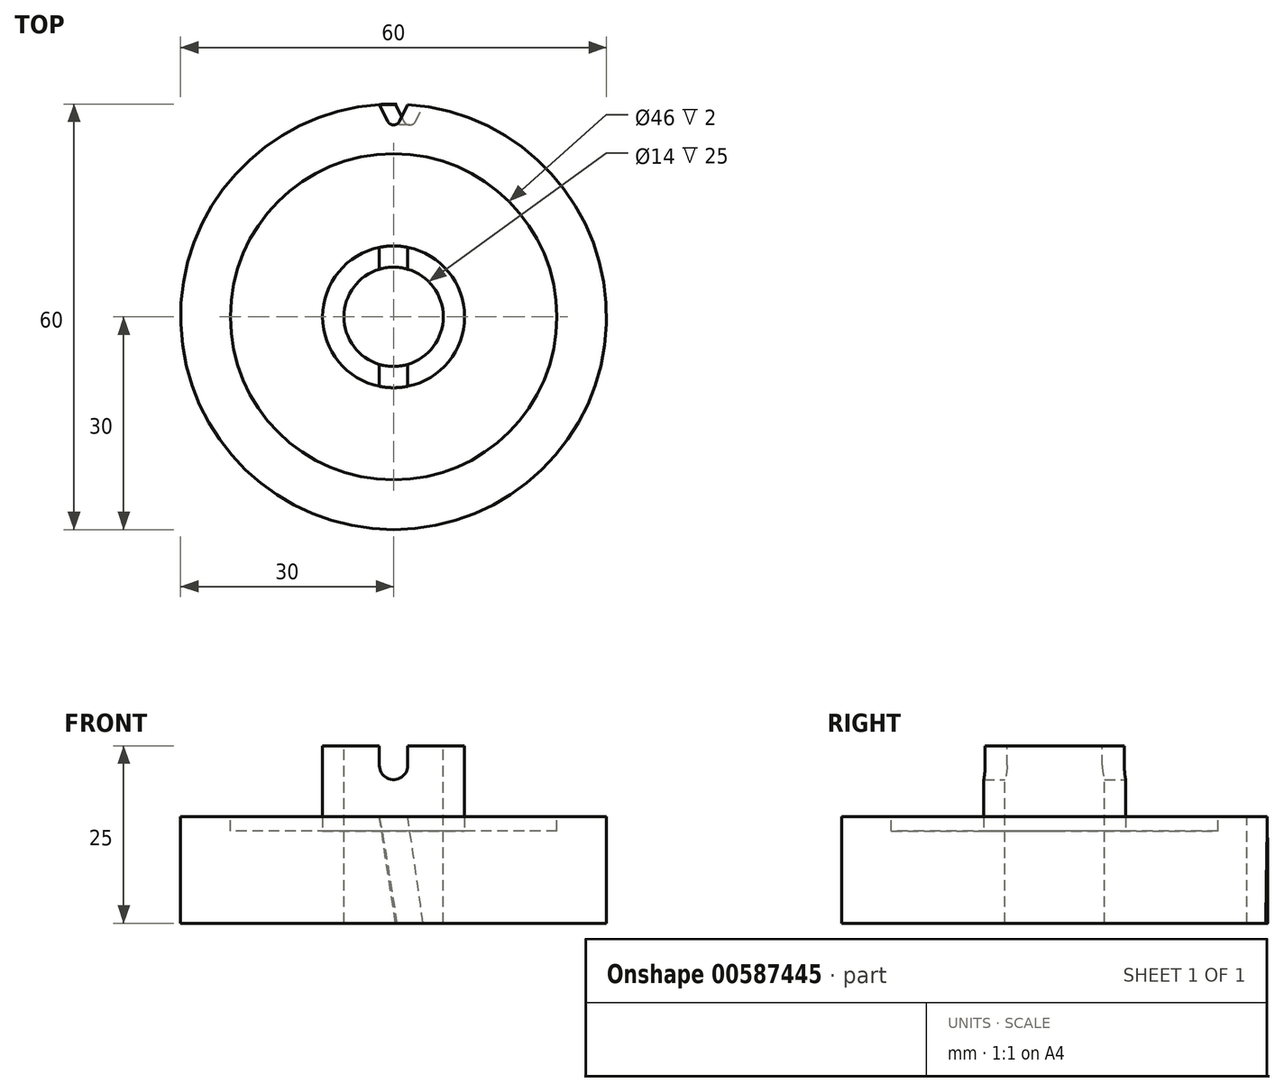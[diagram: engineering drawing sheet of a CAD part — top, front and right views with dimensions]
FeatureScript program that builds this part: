
annotation { "Feature Type Name" : "Feature", "Feature Type Description" : "" }
export const myFeature = defineFeature(function(context is Context, id is Id, definition is map)
    precondition{}
    {
        {
            var Q0;
            Q0=qCreatedBy(makeId("Top.planeOp"),FACE);
            var sketch = newSketch(context, id + "F0", { "sketchPlane" : qUnion([Q0])});
            skCircle(sketch, "E0", {"center": v(0, 0) * mm, "radius": 30 * mm});
            skSolve(sketch);
        }
        {
            var Q0;
            Q0 = qSketchRegion(id + "F0", true);
            extrude(context, id + "F1", {"entities" : qUnion([Q0]), "depth" : 15 * mm, "offsetDistance" : 25 * mm});
        }
        {
            var Q0;
            Q0=makeQuery(id+"F1.opExtrude","CAP_FACE",FACE,{"disambiguationData":[OSD([sQuery(id+"F0.wireOp",EDGE,"E0")])],"isStart":false});
            var sketch = newSketch(context, id + "F2", { "sketchPlane" : qUnion([Q0])});
            skCircle(sketch, "E1.0", {"center": v(0, 0) * mm, "radius": 23 * mm});
            skSolve(sketch);
        }
        {
            var Q0;
            Q0 = qSketchRegion(id + "F2", true);
            extrude(context, id + "F3", {"entities" : qUnion([Q0]), "operationType" : NewBodyOperationType.REMOVE, "oppositeDirection" : true, "depth" : 2 * mm, "offsetDistance" : 25 * mm});
        }
        {
            var Q0;
            Q0=makeQuery(id+"F3.boolean.opBoolean","COPY",FACE,{"derivedFrom":makeQuery(id+"F3.opExtrude","CAP_FACE",FACE,{"disambiguationData":[OSD([sQuery(id+"F2.wireOp",EDGE,"E1.0")])],"isStart":false})});
            var sketch = newSketch(context, id + "F4", { "sketchPlane" : qUnion([Q0])});
            skCircle(sketch, "E2", {"center": v(0, 0) * mm, "radius": 10 * mm});
            skSolve(sketch);
        }
        {
            var Q0;
            Q0=makeQuery(id+"F4.imprint","IMPRINT",FACE,{"disambiguationData":[TD([[makeQuery(id+"F4.imprint","IMPRINT",EDGE,{"derivedFrom":sQuery(id+"F4.wireOp",EDGE,"E2")}),1.0]])]});
            extrude(context, id + "F5", {"entities" : qUnion([Q0]), "operationType" : NewBodyOperationType.ADD, "depth" : 12 * mm, "offsetDistance" : 25 * mm});
        }
        {
            var Q0;
            Q0=makeQuery(id+"F5.opExtrude","CAP_FACE",FACE,{"disambiguationData":[OSD([sQuery(id+"F4.wireOp",EDGE,"E2")])],"isStart":false});
            var sketch = newSketch(context, id + "F6", { "sketchPlane" : qUnion([Q0])});
            skCircle(sketch, "E3.0", {"center": v(0, 0) * mm, "radius": 7 * mm});
            skSolve(sketch);
        }
        {
            var Q0;
            Q0=makeQuery(id+"F6.imprint","IMPRINT",FACE,{"disambiguationData":[TD([[makeQuery(id+"F6.imprint","IMPRINT",EDGE,{"derivedFrom":sQuery(id+"F6.wireOp",EDGE,"E3.0")}),1.0]])]});
            extrude(context, id + "F7", {"entities" : qUnion([Q0]), "operationType" : NewBodyOperationType.REMOVE, "oppositeDirection" : true, "depth" : 45.4 * mm, "offsetDistance" : 25 * mm});
        }
        {
            var Q0;
            Q0=qCreatedBy(makeId("Front.planeOp"),FACE);
            var sketch = newSketch(context, id + "F8", { "sketchPlane" : qUnion([Q0])});
            skLineSegment(sketch, "E4.bottom", {"start": v(2, 26.24) * mm, "end": v(-2, 26.24) * mm});
            skLineSegment(sketch, "E4.left", {"start": v(2, 26.24) * mm, "end": v(2, 22.24) * mm});
            skLineSegment(sketch, "E4.right", {"start": v(-2, 26.24) * mm, "end": v(-2, 22.24) * mm});
            skPoint(sketch, "E4.middle", {"position": v(0, 24.24) * mm});
            skArc(sketch, "E5", {"start": v(-2, 22.24) * mm, "mid": v(0, 20.24) * mm, "end": v(2, 22.24) * mm});
            skSolve(sketch);
        }
        {
            var Q0;
            Q0=makeQuery(id+"F8.imprint","IMPRINT",FACE,{"disambiguationData":[TD([[makeQuery(id+"F8.imprint","IMPRINT",EDGE,{"derivedFrom":sQuery(id+"F8.wireOp",EDGE,"E4.bottom")}),1.0]])]});
            extrude(context, id + "F9", {"entities" : qUnion([Q0]), "operationType" : NewBodyOperationType.REMOVE, "endBound" : BoundingType.SYMMETRIC, "depth" : 25 * mm, "offsetDistance" : 25 * mm});
        }
        {
            var Q0;
            Q0=makeQuery(id+"F1.opExtrude","CAP_FACE",FACE,{"disambiguationData":[OSD([sQuery(id+"F0.wireOp",EDGE,"E0")])],"isStart":false});
            var sketch = newSketch(context, id + "F10", { "sketchPlane" : qUnion([Q0])});
            skArc(sketch, "E6", {"start": v(-0.85, 27.58) * mm, "mid": v(0, 27.06) * mm, "end": v(0.85, 27.58) * mm});
            skLineSegment(sketch, "E7", {"start": v(0.85, 27.58) * mm, "end": v(2, 29.93) * mm});
            skLineSegment(sketch, "E8", {"start": v(0, 30.67) * mm, "end": v(0, 25.54) * mm, "construction": true});
            skLineSegment(sketch, "E9.MirrorCS", {"start": v(-0.85, 27.58) * mm, "end": v(-2, 29.93) * mm});
            skArc(sketch, "E10", {"start": v(2, 29.93) * mm, "mid": v(0, 30.34) * mm, "end": v(-2, 29.93) * mm});
            skSolve(sketch);
        }
        {
            var Q0;
            Q0=qCreatedBy(makeId("Front.planeOp"),FACE);
            var sketch = newSketch(context, id + "F11", { "sketchPlane" : qUnion([Q0])});
            skLineSegment(sketch, "E11", {"start": v(0, -1.28) * mm, "end": v(0, 15.72) * mm});
            skLineSegment(sketch, "E12", {"start": v(0, -1.28) * mm, "end": v(-2.57, 15.72) * mm});
            skLineSegment(sketch, "E13", {"start": v(-2.57, 15.72) * mm, "end": v(0, 15.72) * mm});
            skSolve(sketch);
        }
        {
            var Q0;
            Q0=makeQuery(id+"F10.imprint","IMPRINT",FACE,{"disambiguationData":[TD([[makeQuery(id+"F10.imprint","IMPRINT",EDGE,{"derivedFrom":sQuery(id+"F10.wireOp",EDGE,"E6")}),1.0]])]});
            var Q1;
            {var subQ0=sQuery(id+"F10.wireOp",EDGE,"E10");Q1=makeQuery(id+"F10.imprint","IMPRINT",FACE,{"disambiguationData":[TD([[makeQuery(id+"F10.imprint","IMPRINT",EDGE,{"derivedFrom":subQ0}),1.0]])]});}
            var Q2;
            Q2=sQuery(id+"F11.wireOp",EDGE,"E12");
            sweep(context, id + "F12", {"operationType" : NewBodyOperationType.REMOVE, "profiles" : qUnion([Q0, Q1]), "path" : qUnion([Q2])});
        }
    });
